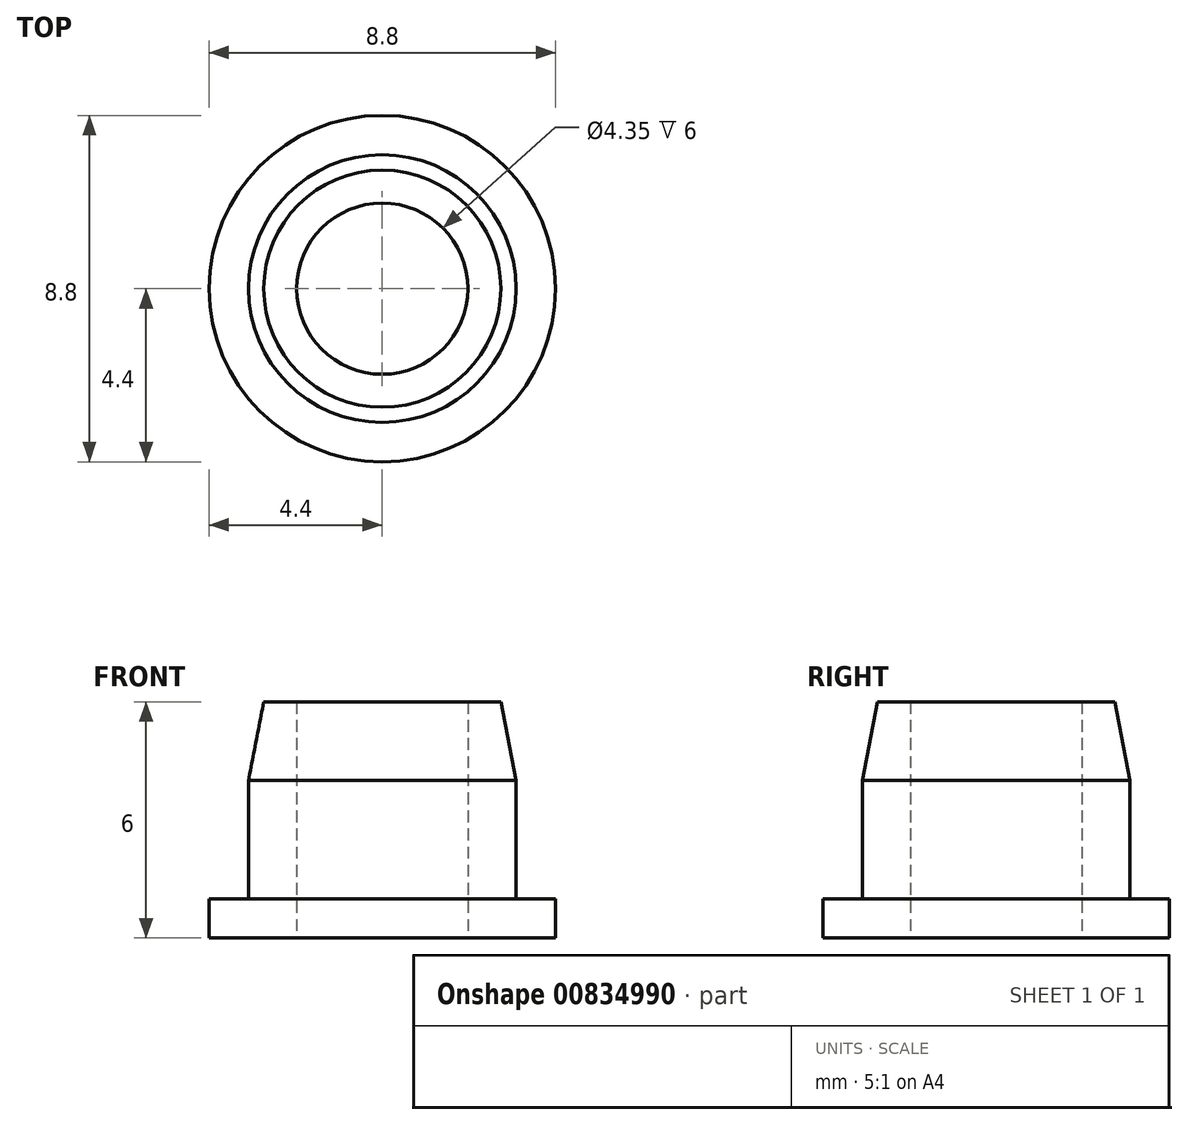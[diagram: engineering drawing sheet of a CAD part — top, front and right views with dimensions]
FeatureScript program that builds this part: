
annotation { "Feature Type Name" : "Feature", "Feature Type Description" : "" }
export const myFeature = defineFeature(function(context is Context, id is Id, definition is map)
    precondition{}
    {
        {
            var Q0;
            Q0=qCreatedBy(makeId("Front.planeOp"),FACE);
            var sketch = newSketch(context, id + "F0", { "sketchPlane" : qUnion([Q0])});
            skLineSegment(sketch, "E0", {"start": v(-2.17, 0) * mm, "end": v(-2.17, 6) * mm});
            skLineSegment(sketch, "E1", {"start": v(-2.17, 6) * mm, "end": v(-3.01, 6) * mm});
            skLineSegment(sketch, "E2", {"start": v(-3.4, 1) * mm, "end": v(-3.4, 4) * mm});
            skLineSegment(sketch, "E3", {"start": v(-3.4, 4) * mm, "end": v(-3.01, 6) * mm});
            skLineSegment(sketch, "E4", {"start": v(0, 0) * mm, "end": v(0, 17.16) * mm, "construction": true});
            skLineSegment(sketch, "E5", {"start": v(-2.17, 0) * mm, "end": v(-3.4, 0) * mm});
            skLineSegment(sketch, "E6", {"start": v(-3.4, 0) * mm, "end": v(-4.4, 0) * mm});
            skLineSegment(sketch, "E7", {"start": v(-4.4, 0) * mm, "end": v(-4.4, 1) * mm});
            skLineSegment(sketch, "E8", {"start": v(-4.4, 1) * mm, "end": v(-3.4, 1) * mm});
            skSolve(sketch);
        }
        {
            var Q0;
            Q0 = qSketchRegion(id + "F0", true);
            var Q1;
            Q1=sQuery(id+"F0.wireOp",EDGE,"E4");
            revolve(context, id + "F1", {"surfaceOperationType" : NewSurfaceOperationType.NEW, "entities" : qUnion([Q0]), "axis" : qUnion([Q1]), "revolveType" : RevolveType.FULL});
        }
    });
